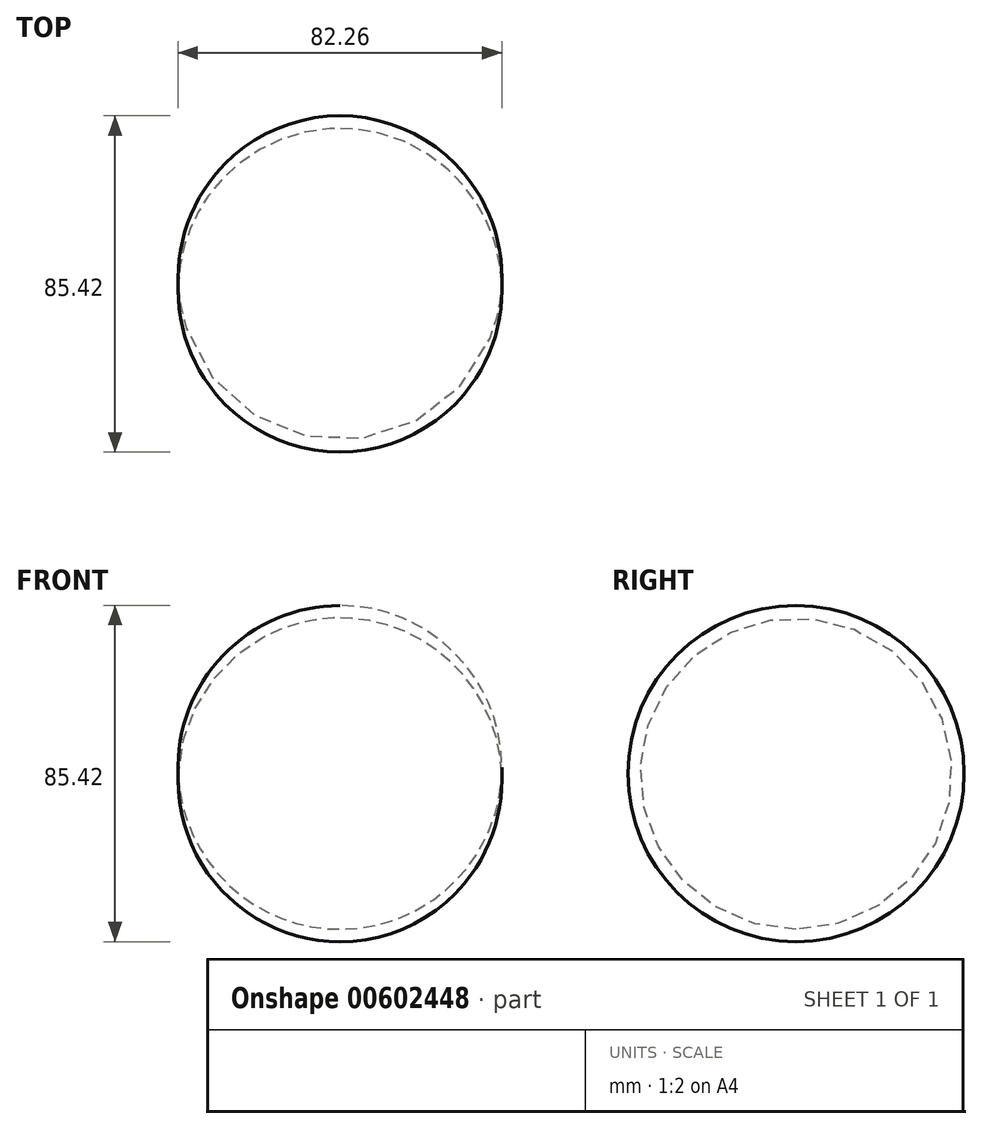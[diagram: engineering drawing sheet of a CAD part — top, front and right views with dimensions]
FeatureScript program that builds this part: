
annotation { "Feature Type Name" : "Feature", "Feature Type Description" : "" }
export const myFeature = defineFeature(function(context is Context, id is Id, definition is map)
    precondition{}
    {
        {
            var Q0;
            Q0=qCreatedBy(makeId("Front.planeOp"),FACE);
            var sketch = newSketch(context, id + "F0", { "sketchPlane" : qUnion([Q0])});
            skArc(sketch, "E0", {"start": v(40.23, 0) * mm, "mid": v(-0.87, 42.7) * mm, "end": v(-41.97, 0) * mm});
            skLineSegment(sketch, "E1", {"start": v(-41.97, 0) * mm, "end": v(40.23, 0) * mm});
            skSolve(sketch);
        }
        {
            var Q0;
            Q0=makeQuery(id+"F0.imprint","IMPRINT",FACE,{"disambiguationData":[TD([[makeQuery(id+"F0.imprint","IMPRINT",EDGE,{"derivedFrom":sQuery(id+"F0.wireOp",EDGE,"E0")}),1.0]])]});
            var Q1;
            Q1=sQuery(id+"F0.wireOp",EDGE,"E1");
            revolve(context, id + "F1", {"entities" : qUnion([Q0]), "axis" : qUnion([Q1]), "revolveType" : RevolveType.FULL});
        }
    });
